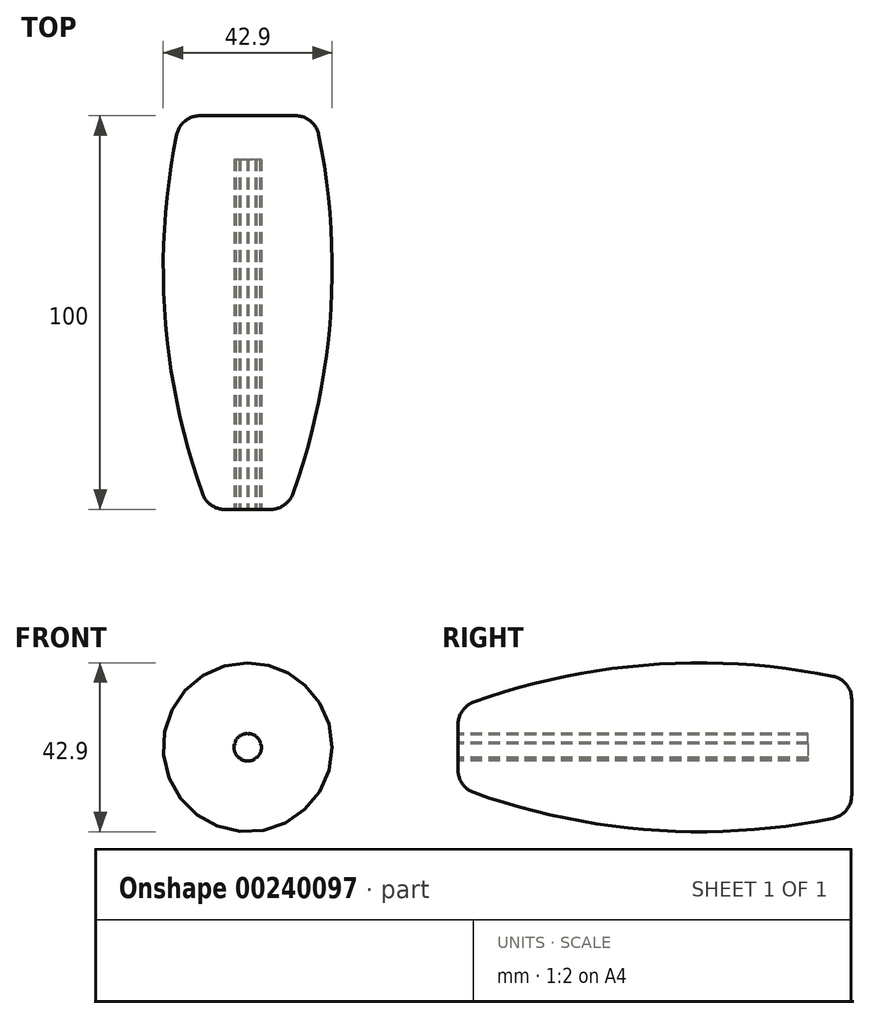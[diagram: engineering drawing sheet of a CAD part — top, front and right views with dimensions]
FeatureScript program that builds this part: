
annotation { "Feature Type Name" : "Feature", "Feature Type Description" : "" }
export const myFeature = defineFeature(function(context is Context, id is Id, definition is map)
    precondition{}
    {
        {
            var Q0;
            Q0=qCreatedBy(makeId("Top.planeOp"),FACE);
            var sketch = newSketch(context, id + "F0", { "sketchPlane" : qUnion([Q0])});
            skLineSegment(sketch, "E0", {"start": v(0, 0) * mm, "end": v(0, 100) * mm});
            skLineSegment(sketch, "E1", {"start": v(0, 0) * mm, "end": v(10, 0) * mm});
            skLineSegment(sketch, "E2", {"start": v(0, 100) * mm, "end": v(17, 100) * mm});
            skArc(sketch, "E3", {"start": v(10, 0) * mm, "mid": v(21.04, 49.47) * mm, "end": v(17, 100) * mm});
            skSolve(sketch);
        }
        {
            var Q0;
            Q0=makeQuery(id+"F0.imprint","IMPRINT",FACE,{"disambiguationData":[TD([[makeQuery(id+"F0.imprint","IMPRINT",EDGE,{"derivedFrom":sQuery(id+"F0.wireOp",EDGE,"E0")}),-1.0]])]});
            var Q1;
            Q1=sQuery(id+"F0.wireOp",EDGE,"E0");
            revolve(context, id + "F1", {"entities" : qUnion([Q0]), "axis" : qUnion([Q1]), "revolveType" : RevolveType.FULL});
        }
        {
            var Q0;
            Q0=makeQuery(id+"F1.opRevolve","SWEPT_FACE",FACE,{"disambiguationData":[OSD([sQuery(id+"F0.wireOp",EDGE,"E1")])]});
            var sketch = newSketch(context, id + "F2", { "sketchPlane" : qUnion([Q0])});
            skPoint(sketch, "E4.0", {"position": v(0, 0) * mm});
            skArc(sketch, "E5", {"start": v(-0.23, 3.5) * mm, "mid": v(-2.06, 2.83) * mm, "end": v(-3.25, 1.3) * mm});
            skLineSegment(sketch, "E6", {"start": v(0, 3.5) * mm, "end": v(0, 3.1) * mm, "construction": true});
            skLineSegment(sketch, "E7", {"start": v(0, 3.1) * mm, "end": v(0.23, 3.5) * mm});
            skLineSegment(sketch, "E8", {"start": v(0, 3.1) * mm, "end": v(-0.23, 3.5) * mm});
            skLineSegment(sketch, "E9.1.0", {"start": v(-2.95, 0.96) * mm, "end": v(-3.4, 0.86) * mm});
            skLineSegment(sketch, "E9.1.1", {"start": v(-2.95, 0.96) * mm, "end": v(-3.25, 1.3) * mm});
            skLineSegment(sketch, "E9.1.2", {"start": v(-3.33, 1.08) * mm, "end": v(-2.95, 0.96) * mm, "construction": true});
            skLineSegment(sketch, "E9.2.0", {"start": v(-1.82, -2.5) * mm, "end": v(-1.87, -2.96) * mm});
            skLineSegment(sketch, "E9.2.1", {"start": v(-1.82, -2.5) * mm, "end": v(-2.24, -2.7) * mm});
            skLineSegment(sketch, "E9.2.2", {"start": v(-2.06, -2.83) * mm, "end": v(-1.82, -2.5) * mm, "construction": true});
            skLineSegment(sketch, "E9.3.0", {"start": v(1.82, -2.5) * mm, "end": v(2.24, -2.7) * mm});
            skLineSegment(sketch, "E9.3.1", {"start": v(1.82, -2.5) * mm, "end": v(1.87, -2.96) * mm});
            skLineSegment(sketch, "E9.3.2", {"start": v(2.06, -2.83) * mm, "end": v(1.82, -2.5) * mm, "construction": true});
            skLineSegment(sketch, "E9.4.0", {"start": v(2.95, 0.96) * mm, "end": v(3.25, 1.3) * mm});
            skLineSegment(sketch, "E9.4.1", {"start": v(2.95, 0.96) * mm, "end": v(3.4, 0.86) * mm});
            skLineSegment(sketch, "E9.4.2", {"start": v(3.33, 1.08) * mm, "end": v(2.95, 0.96) * mm, "construction": true});
            skArc(sketch, "E10.trimOffspring", {"start": v(3.25, 1.3) * mm, "mid": v(2.06, 2.83) * mm, "end": v(0.23, 3.5) * mm});
            skArc(sketch, "E11.trimOffspring", {"start": v(2.24, -2.7) * mm, "mid": v(3.33, -1.08) * mm, "end": v(3.4, 0.86) * mm});
            skArc(sketch, "E12.trimOffspring", {"start": v(-1.87, -2.96) * mm, "mid": v(0, -3.5) * mm, "end": v(1.87, -2.96) * mm});
            skArc(sketch, "E13.trimOffspring", {"start": v(-3.4, 0.86) * mm, "mid": v(-3.33, -1.08) * mm, "end": v(-2.24, -2.7) * mm});
            skSolve(sketch);
        }
        {
            var Q0;
            Q0=makeQuery(id+"F2.imprint","IMPRINT",FACE,{"disambiguationData":[TD([[makeQuery(id+"F2.imprint","IMPRINT",EDGE,{"derivedFrom":sQuery(id+"F2.wireOp",EDGE,"E5")}),1.0]])]});
            extrude(context, id + "F3", {"entities" : qUnion([Q0]), "operationType" : NewBodyOperationType.REMOVE, "oppositeDirection" : true, "depth" : 88.9 * mm});
        }
        {
            var Q0;
            Q0=makeQuery(id+"F1.opRevolve","SWEPT_EDGE",EDGE,{"disambiguationData":[OSD([sQuery(id+"F0.wireOp",EDGE,"E1"),sQuery(id+"F0.wireOp",EDGE,"E3")])]});
            var Q1;
            Q1=makeQuery(id+"F1.opRevolve","SWEPT_EDGE",EDGE,{"disambiguationData":[OSD([sQuery(id+"F0.wireOp",EDGE,"E2"),sQuery(id+"F0.wireOp",EDGE,"E3")])]});
            fillet(context, id + "F4", {"entities" : qUnion([Q0, Q1]), "radius" : 6 * mm, "tangentPropagation" : true, "allowEdgeOverflow" : false});
        }
    });
